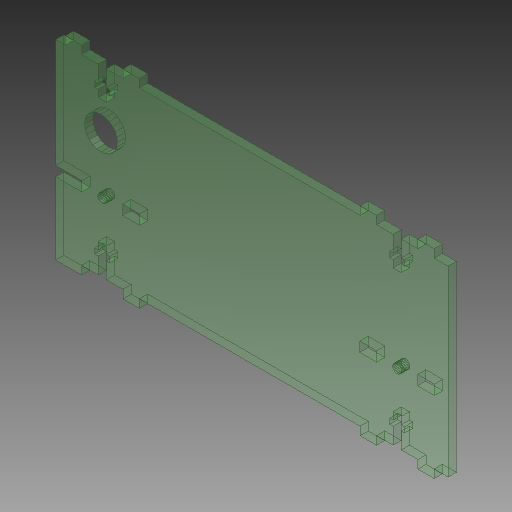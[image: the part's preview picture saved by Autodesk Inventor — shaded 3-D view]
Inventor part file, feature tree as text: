
AUTODESK INVENTOR PART (.ipt)
format: ipt  version: 2017 (Build 210142000, 142)  size: 293,888 bytes
history: native  units: mm
features: extrude x1, sketch x1
ambient origin geometry x8: Origin, YZ Plane, XZ Plane, XY Plane, X Axis, Y Axis, Z Axis, Center Point
bodies: Solid1 (feature_tree)
feature tree (2):
  extrude  "Extrusion1"  [1 undecoded]
  sketch  "Sketch1"  dims[d0=3.0mm d1=0.0mm]
note: 1 required parameter value undecoded (feature->parameter linkage not recoverable at this tier; creation-order binding heuristic only, values carry confidence <= 0.55)
